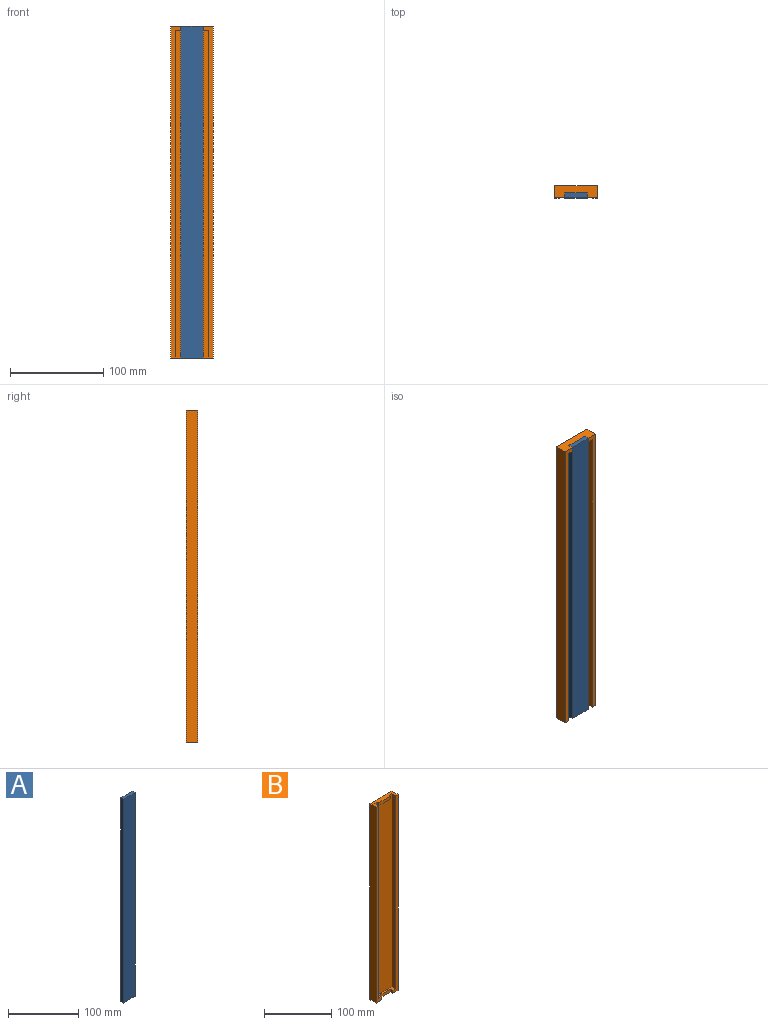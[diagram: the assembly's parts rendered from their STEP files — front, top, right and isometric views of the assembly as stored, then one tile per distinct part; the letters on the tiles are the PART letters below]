
ASSEMBLY  parts=2 mates=1
PART A: 6 faces, bbox 24.1x5.2x355.6 mm
  f0: plane 355.6x24.13mm, normal (0,1,0), area 8580.6mm2, adj f1,f3,f4,f5
  f1: plane 355.6x5.21mm, normal (-1,0,0), area 1851.6mm2, adj f0,f2,f4,f5
  f2: plane 355.6x24.13mm, normal (0,-1,0), area 8580.6mm2, adj f1,f3,f4,f5
  f3: plane 355.6x5.21mm, normal (1,0,0), area 1851.6mm2, adj f0,f2,f4,f5
  f4: plane 24.13x5.21mm, normal (0,0,-1), area 125.6mm2, adj f0,f1,f2,f3
  f5: plane 24.13x5.21mm, normal (0,0,1), area 125.6mm2, adj f0,f1,f2,f3
PART B: 18 faces, bbox 46x12.8x355.6 mm
  f0: plane 355.6x10.92mm, normal (0,-1,0), area 1836.1mm2, adj f1,f3,f4,f5,f8,f12
  f1: plane 35.81x7.75mm, normal (0,0,1), area 151.8mm2, adj f0,f2,f8,f9,f10,f11,f12,f13
  f2: plane 355.6x10.92mm, normal (0,-1,0), area 1836.1mm2, adj f1,f3,f5,f6,f9,f13
  f3: plane 45.97x12.83mm, normal (0,0,1), area 373.5mm2, adj f0,f2,f4,f6,f7,f8,f9,f10
  f4: plane 355.6x12.83mm, normal (-1,0,0), area 4561.3mm2, adj f0,f3,f5,f7
  f5: plane 45.97x12.83mm, normal (0,0,-1), area 464.1mm2, adj f0,f2,f4,f6,f7,f11,f12,f13
  f6: plane 355.6x12.83mm, normal (1,0,0), area 4561.3mm2, adj f2,f3,f5,f7
  f7: plane 355.6x45.97mm, normal (0,1,0), area 16348.4mm2, adj f3,f4,f5,f6
  f8: plane 350.52x7.75mm, normal (1,0,0), area 2715.5mm2, adj f0,f1,f3,f10
  f9: plane 350.52x7.75mm, normal (-1,0,0), area 2715.5mm2, adj f1,f2,f3,f10
  f10: plane 350.52x35.81mm, normal (0,-1,0), area 12430.9mm2, adj f1,f3,f8,f9,f15,f16,f17
  f11: plane 24.13x5.08mm, normal (0,-1,0), area 122.6mm2, adj f1,f5,f12,f13
  f12: plane 5.21x5.08mm, normal (1,0,0), area 26.5mm2, adj f0,f1,f5,f11
  f13: plane 5.21x5.08mm, normal (-1,0,0), area 26.5mm2, adj f1,f2,f5,f11
  f14: plane 24.13x5.08mm, normal (0,-1,0), area 122.6mm2, adj f3,f15,f16,f17
  f15: plane 5.08x2.54mm, normal (1,0,0), area 12.9mm2, adj f3,f10,f14,f17
  f16: plane 5.08x2.54mm, normal (-1,0,0), area 12.9mm2, adj f3,f10,f14,f17
  f17: plane 24.13x2.54mm, normal (0,0,-1), area 61.3mm2, adj f10,f14,f15,f16
PLACE A rot(axis=(0,-1,0),180deg) t=(-203.31,216.57,795.93)mm
PLACE B rot(axis=(0,-1,0),180deg) t=(-203.31,216.57,795.93)mm
MATE slider B.f3 <-> A.f5  axis (0,0,-1) through (-226.3,208.95,440.33)mm
